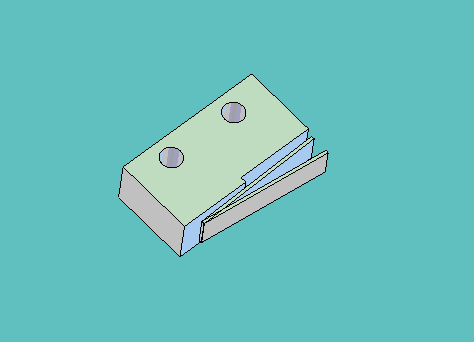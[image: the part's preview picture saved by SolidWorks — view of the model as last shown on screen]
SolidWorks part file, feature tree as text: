
SOLIDWORKS PART (.sldprt)
format: sldprt  version: not decoded by parser v0  size: 962,560 bytes
history: native  units: mm
features: sketch x7, extrude x7, material x1, boolean_combine x1, plane x1 (+11 scaffold rows collapsed)
feature tree (28):
  scaffold x11  (default folders/planes/origin — collapsed)
  material  "Material <not specified>"
  sketch  "Sketch3"  dims[c1.D1=19.685mm c1.D2=9.525mm c1.D3=3.175mm c1.D4=17.4625mm c2.D3=~17.62125mm c2.D4=3.175mm]
  extrude  "Extrude3"  Depth=6.35mm
  sketch  "Sketch4"  dims[D4=~2.77622mm D5=~2.77622mm D1=2.54mm D2=5.08mm D3=9.525mm]
  extrude  "Extrude4"  [1 undecoded]
  boolean_combine  "Combine2"
  sketch  "Sketch5"  dims[D1=~0.79375mm D2=~10.31875mm]
  extrude  "Extrude5"  [1 undecoded]
  plane  "Plane1"  Offset=0.79375mm
  sketch  "Sketch6"  dims[c1.D1=~2.38125mm c1.D2=~0.79375mm c1.D3=3.175mm c1.D4=0.4064mm c2.D3=13.7668mm]
  extrude  "min"  Depth=3.96875mm
  sketch  "Sketch7"  dims[c1.D1=~2.38125mm c1.D2=~0.79375mm c1.D3=3.175mm c1.D4=0.4064mm c2.D3=11.4808mm]
  extrude  "turn on"  Depth=3.96875mm
  sketch  "Sketch8"  dims[c1.D1=~2.38125mm c1.D2=~0.79375mm c1.D3=3.175mm c1.D4=0.4064mm c2.D3=12.573mm]
  extrude  "turn off"  Depth=3.96875mm
  sketch  "Sketch9"  dims[c1.D1=~2.38125mm c1.D2=~0.79375mm c1.D3=3.175mm c1.D4=0.4064mm c2.D3=10.16mm]
  extrude  "max"  Depth=3.96875mm
decode coverage: 12 of 15 modeling features carry decoded parameters
note: ~ marks probable driven/reference dimensions
note: 2 parameter values undecoded
note: suppression state not decoded; provenance and decode notes live in map.json
